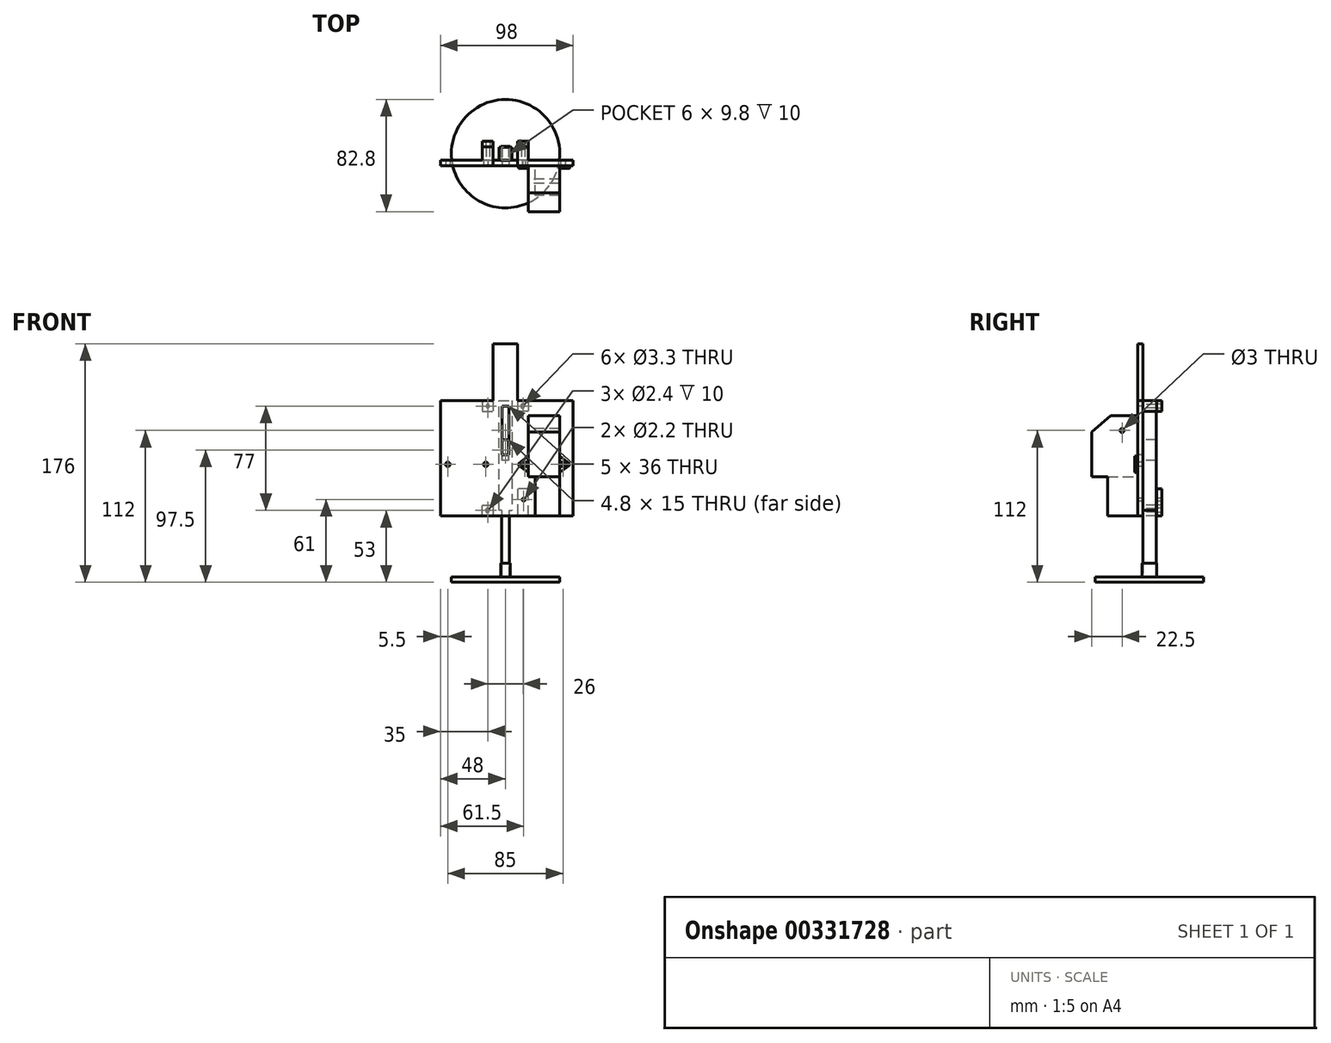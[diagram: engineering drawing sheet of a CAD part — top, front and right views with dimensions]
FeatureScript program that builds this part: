
annotation { "Feature Type Name" : "Feature", "Feature Type Description" : "" }
export const myFeature = defineFeature(function(context is Context, id is Id, definition is map)
    precondition{}
    {
        {
            var Q0;
            Q0=qCreatedBy(makeId("Right.planeOp"),FACE);
            var sketch = newSketch(context, id + "F0", { "sketchPlane" : qUnion([Q0])});
            skLineSegment(sketch, "E0", {"start": v(0, 0) * mm, "end": v(0, 74) * mm});
            skLineSegment(sketch, "E1", {"start": v(0, 74) * mm, "end": v(-20, 74) * mm});
            skLineSegment(sketch, "E2", {"start": v(-20, 74) * mm, "end": v(-34, 74) * mm, "construction": true});
            skLineSegment(sketch, "E3", {"start": v(-34, 74) * mm, "end": v(-34, 73) * mm, "construction": true});
            skLineSegment(sketch, "E4", {"start": v(-34, 73) * mm, "end": v(-34, 62) * mm, "construction": true});
            skLineSegment(sketch, "E5", {"start": v(-34, 62) * mm, "end": v(-20, 74) * mm});
            skLineSegment(sketch, "E6", {"start": v(-34, 62) * mm, "end": v(-34, 29) * mm});
            skLineSegment(sketch, "E7", {"start": v(-34, 29) * mm, "end": v(-22, 29) * mm});
            skLineSegment(sketch, "E8", {"start": v(-22, 29) * mm, "end": v(-22, 0) * mm});
            skLineSegment(sketch, "E9", {"start": v(-22, 0) * mm, "end": v(0, 0) * mm});
            skLineSegment(sketch, "E10", {"start": v(0, 74) * mm, "end": v(-11.5, 74) * mm, "construction": true});
            skLineSegment(sketch, "E11", {"start": v(-11.5, 74) * mm, "end": v(-11.5, 63) * mm, "construction": true});
            skCircle(sketch, "E12", {"center": v(-11.5, 63) * mm, "radius": 1.5 * mm});
            skSolve(sketch);
        }
        {
            var Q0;
            Q0 = qSketchRegion(id + "F0", true);
            extrude(context, id + "F1", {"entities" : qUnion([Q0]), "depth" : 23 * mm});
        }
        {
            var Q0;
            Q0=makeQuery(id+"F1.opExtrude","CAP_FACE",FACE,{"disambiguationData":[OSD([sQuery(id+"F0.wireOp",EDGE,"E0"),sQuery(id+"F0.wireOp",EDGE,"E1"),sQuery(id+"F0.wireOp",EDGE,"E5"),sQuery(id+"F0.wireOp",EDGE,"E6"),sQuery(id+"F0.wireOp",EDGE,"E7"),sQuery(id+"F0.wireOp",EDGE,"E8"),sQuery(id+"F0.wireOp",EDGE,"E9"),sQuery(id+"F0.wireOp",EDGE,"E12")])],"isStart":true});
            var sketch = newSketch(context, id + "F2", { "sketchPlane" : qUnion([Q0])});
            skLineSegment(sketch, "E13", {"start": v(22, 29) * mm, "end": v(0, 29) * mm});
            skLineSegment(sketch, "E14", {"start": v(0, 29) * mm, "end": v(0, 0) * mm});
            skLineSegment(sketch, "E15", {"start": v(0, 0) * mm, "end": v(22, 0) * mm});
            skLineSegment(sketch, "E16", {"start": v(22, 0) * mm, "end": v(22, 29) * mm});
            skSolve(sketch);
        }
        {
            var Q0;
            Q0 = qSketchRegion(id + "F2", true);
            extrude(context, id + "F3", {"entities" : qUnion([Q0]), "operationType" : NewBodyOperationType.REMOVE, "oppositeDirection" : true, "depth" : 5 * mm});
        }
        {
            var Q0;
            Q0=makeQuery(id+"F1.opExtrude","SWEPT_FACE",FACE,{"disambiguationData":[OSD([sQuery(id+"F0.wireOp",EDGE,"E0")])]});
            var sketch = newSketch(context, id + "F4", { "sketchPlane" : qUnion([Q0])});
            skLineSegment(sketch, "E17", {"start": v(0, 74) * mm, "end": v(0, 38) * mm, "construction": true});
            skLineSegment(sketch, "E18", {"start": v(0, 38) * mm, "end": v(8, 38) * mm, "construction": true});
            skLineSegment(sketch, "E19", {"start": v(0, 38) * mm, "end": v(-31, 38) * mm, "construction": true});
            skLineSegment(sketch, "E20", {"start": v(0, 38) * mm, "end": v(0, 32) * mm, "construction": true});
            skLineSegment(sketch, "E21", {"start": v(0, 38) * mm, "end": v(0, 44) * mm, "construction": true});
            skLineSegment(sketch, "E22", {"start": v(-23, 38) * mm, "end": v(-23, 44) * mm, "construction": true});
            skLineSegment(sketch, "E23", {"start": v(-23, 38) * mm, "end": v(-23, 32) * mm, "construction": true});
            skLineSegment(sketch, "E24", {"start": v(-23, 44) * mm, "end": v(-29.93, 38.8) * mm});
            skLineSegment(sketch, "E25", {"start": v(-23, 32) * mm, "end": v(-29.93, 37.2) * mm});
            skLineSegment(sketch, "E26", {"start": v(0, 32) * mm, "end": v(6.93, 37.2) * mm});
            skLineSegment(sketch, "E27", {"start": v(6.93, 38.8) * mm, "end": v(0, 44) * mm});
            skLineSegment(sketch, "E28", {"start": v(-23, 44) * mm, "end": v(-23, 32) * mm});
            skLineSegment(sketch, "E29", {"start": v(0, 44) * mm, "end": v(0, 32) * mm});
            skPoint(sketch, "E30.visualSharp", {"position": v(-31, 38) * mm});
            skArc(sketch, "E30.filletArc", {"start": v(-29.93, 38.8) * mm, "mid": v(-30.33, 38) * mm, "end": v(-29.93, 37.2) * mm});
            skPoint(sketch, "E31.visualSharp", {"position": v(8, 38) * mm});
            skArc(sketch, "E31.filletArc", {"start": v(6.93, 37.2) * mm, "mid": v(7.33, 38) * mm, "end": v(6.93, 38.8) * mm});
            skLineSegment(sketch, "E32", {"start": v(-23, 38) * mm, "end": v(-23, 39.5) * mm, "construction": true});
            skLineSegment(sketch, "E33", {"start": v(-23, 39.5) * mm, "end": v(-28, 39.5) * mm, "construction": true});
            skLineSegment(sketch, "E34", {"start": v(-28, 39.5) * mm, "end": v(-28, 36.5) * mm, "construction": true});
            skLineSegment(sketch, "E35", {"start": v(-28, 36.5) * mm, "end": v(-23, 36.5) * mm, "construction": true});
            skLineSegment(sketch, "E36", {"start": v(-23, 39.5) * mm, "end": v(-28, 39.5) * mm});
            skLineSegment(sketch, "E37", {"start": v(-28, 36.5) * mm, "end": v(-23, 36.5) * mm});
            skLineSegment(sketch, "E38", {"start": v(-28, 36.5) * mm, "end": v(-28, 39.5) * mm});
            skLineSegment(sketch, "E39", {"start": v(0, 38) * mm, "end": v(0, 39.5) * mm, "construction": true});
            skLineSegment(sketch, "E40", {"start": v(0, 38) * mm, "end": v(0, 36.5) * mm, "construction": true});
            skLineSegment(sketch, "E41", {"start": v(0, 39.5) * mm, "end": v(5, 39.5) * mm});
            skLineSegment(sketch, "E42", {"start": v(5, 39.5) * mm, "end": v(5, 36.5) * mm});
            skLineSegment(sketch, "E43", {"start": v(5, 36.5) * mm, "end": v(0, 36.5) * mm});
            skSolve(sketch);
        }
        {
            var Q0;
            {var subQ4=sQuery(id+"F4.wireOp",EDGE,"E26");Q0=makeQuery(id+"F4.imprint","IMPRINT",FACE,{"disambiguationData":[TD([[makeQuery(id+"F4.imprint","IMPRINT",EDGE,{"derivedFrom":subQ4}),1.0]])]});}
            var Q1;
            {var subQ4=sQuery(id+"F4.wireOp",EDGE,"E24");Q1=makeQuery(id+"F4.imprint","IMPRINT",FACE,{"disambiguationData":[TD([[makeQuery(id+"F4.imprint","IMPRINT",EDGE,{"derivedFrom":subQ4}),1.0]])]});}
            extrude(context, id + "F5", {"entities" : qUnion([Q0, Q1]), "operationType" : NewBodyOperationType.ADD, "oppositeDirection" : true, "depth" : 2 * mm});
        }
        {
            var Q0;
            Q0=makeQuery(id+"F5.boolean.opBoolean","MERGE",FACE,{"derivedFrom":[makeQuery(id+"F1.opExtrude","SWEPT_FACE",FACE,{"disambiguationData":[OSD([sQuery(id+"F0.wireOp",EDGE,"E0")])]}),makeQuery(id+"F5.opExtrude","CAP_FACE",FACE,{"disambiguationData":[OSD([sQuery(id+"F4.wireOp",EDGE,"E24"),sQuery(id+"F4.wireOp",EDGE,"E25"),sQuery(id+"F4.wireOp",EDGE,"E28"),sQuery(id+"F4.wireOp",EDGE,"E30.filletArc"),sQuery(id+"F4.wireOp",EDGE,"E36"),sQuery(id+"F4.wireOp",EDGE,"E37"),sQuery(id+"F4.wireOp",EDGE,"E38")])],"isStart":true}),makeQuery(id+"F5.opExtrude","CAP_FACE",FACE,{"disambiguationData":[OSD([sQuery(id+"F4.wireOp",EDGE,"E26"),sQuery(id+"F4.wireOp",EDGE,"E27"),sQuery(id+"F4.wireOp",EDGE,"E29"),sQuery(id+"F4.wireOp",EDGE,"E31.filletArc"),sQuery(id+"F4.wireOp",EDGE,"E41"),sQuery(id+"F4.wireOp",EDGE,"E42"),sQuery(id+"F4.wireOp",EDGE,"E43")])],"isStart":true})]});
            var sketch = newSketch(context, id + "F6", { "sketchPlane" : qUnion([Q0])});
            skLineSegment(sketch, "E44", {"start": v(-29.93, 38.8) * mm, "end": v(-29.93, 37.2) * mm, "construction": true});
            skLineSegment(sketch, "E45", {"start": v(-29.93, 37.2) * mm, "end": v(-29.93, 38) * mm, "construction": true});
            skLineSegment(sketch, "E46", {"start": v(-29.93, 38) * mm, "end": v(11.6, 38) * mm, "construction": true});
            skPoint(sketch, "E46.endSnap0", {"position": v(7.33, 38) * mm});
            skLineSegment(sketch, "E47", {"start": v(65, 38) * mm, "end": v(-34.09, 38) * mm, "construction": true});
            skLineSegment(sketch, "E48", {"start": v(0, 74) * mm, "end": v(0, 79) * mm, "construction": true});
            skLineSegment(sketch, "E49", {"start": v(0, 79) * mm, "end": v(17, 79) * mm, "construction": true});
            skLineSegment(sketch, "E50", {"start": v(17, 79) * mm, "end": v(17, -51) * mm, "construction": true});
            skLineSegment(sketch, "E51", {"start": v(17, -51) * mm, "end": v(-33, -51) * mm, "construction": true});
            skLineSegment(sketch, "E52", {"start": v(-33, -51) * mm, "end": v(-33, 79) * mm, "construction": true});
            skLineSegment(sketch, "E53", {"start": v(-33, 79) * mm, "end": v(0, 79) * mm, "construction": true});
            skLineSegment(sketch, "E54.top", {"start": v(-33, 0) * mm, "end": v(65, 0) * mm});
            skLineSegment(sketch, "E54.left", {"start": v(-33, 79) * mm, "end": v(-33, 0) * mm});
            skLineSegment(sketch, "E54.right", {"start": v(65, 85) * mm, "end": v(65, 0) * mm});
            skLineSegment(sketch, "E55", {"start": v(17, 38) * mm, "end": v(2.5, 38) * mm, "construction": true});
            skPoint(sketch, "E55.startSnap0", {"position": v(15.46, 38) * mm});
            skLineSegment(sketch, "E56", {"start": v(2.5, 38) * mm, "end": v(-25.5, 38) * mm, "construction": true});
            skCircle(sketch, "E57", {"center": v(-25.5, 38) * mm, "radius": 1.65 * mm});
            skCircle(sketch, "E58", {"center": v(2.5, 38) * mm, "radius": 1.65 * mm});
            skLineSegment(sketch, "E59", {"start": v(17, 38) * mm, "end": v(31.5, 38) * mm, "construction": true});
            skLineSegment(sketch, "E60", {"start": v(31.5, 38) * mm, "end": v(59.5, 38) * mm, "construction": true});
            skCircle(sketch, "E61", {"center": v(31.5, 38) * mm, "radius": 1.65 * mm});
            skCircle(sketch, "E62", {"center": v(59.5, 38) * mm, "radius": 1.65 * mm});
            skLineSegment(sketch, "E63", {"start": v(0, 74) * mm, "end": v(0, 63) * mm, "construction": true});
            skLineSegment(sketch, "E64", {"start": v(0, 63) * mm, "end": v(17, 63) * mm, "construction": true});
            skLineSegment(sketch, "E65", {"start": v(17, 63) * mm, "end": v(17, 45) * mm, "construction": true});
            skLineSegment(sketch, "E66", {"start": v(17, 63) * mm, "end": v(17, 81) * mm, "construction": true});
            skLineSegment(sketch, "E67", {"start": v(-33, 79) * mm, "end": v(-33, 85) * mm});
            skLineSegment(sketch, "E68", {"start": v(-33, 85) * mm, "end": v(65, 85) * mm});
            skLineSegment(sketch, "E69", {"start": v(17, 81) * mm, "end": v(19.5, 81) * mm});
            skLineSegment(sketch, "E70", {"start": v(17, 45) * mm, "end": v(19.5, 45) * mm});
            skLineSegment(sketch, "E71", {"start": v(19.5, 45) * mm, "end": v(19.5, 81) * mm});
            skLineSegment(sketch, "E72", {"start": v(17, 81) * mm, "end": v(14.5, 81) * mm});
            skLineSegment(sketch, "E73", {"start": v(14.5, 81) * mm, "end": v(14.5, 45) * mm});
            skLineSegment(sketch, "E74", {"start": v(14.5, 45) * mm, "end": v(17, 45) * mm});
            skLineSegment(sketch, "E75", {"start": v(17, 81) * mm, "end": v(17, 85) * mm, "construction": true});
            skLineSegment(sketch, "E76", {"start": v(17, 85) * mm, "end": v(17, 127) * mm, "construction": true});
            skLineSegment(sketch, "E77", {"start": v(17, 127) * mm, "end": v(8, 127) * mm});
            skLineSegment(sketch, "E78", {"start": v(8, 127) * mm, "end": v(8, 85) * mm});
            skLineSegment(sketch, "E79", {"start": v(17, 127) * mm, "end": v(26, 127) * mm});
            skLineSegment(sketch, "E80", {"start": v(26, 127) * mm, "end": v(26, 85) * mm});
            skLineSegment(sketch, "E81", {"start": v(2.5, 38) * mm, "end": v(2.5, 12) * mm, "construction": true});
            skLineSegment(sketch, "E82", {"start": v(2.5, 12) * mm, "end": v(3.5, 12) * mm, "construction": true});
            skCircle(sketch, "E83", {"center": v(3.5, 12) * mm, "radius": 1.1 * mm});
            skSolve(sketch);
        }
        {
            var Q0;
            Q0 = qSketchRegion(id + "F6", true);
            extrude(context, id + "F7", {"entities" : qUnion([Q0]), "depth" : 4 * mm});
        }
        {
            var Q0;
            Q0=makeQuery(id+"F7.opExtrude","CAP_FACE",FACE,{"disambiguationData":[OSD([sQuery(id+"F6.wireOp",EDGE,"E54.top"),sQuery(id+"F6.wireOp",EDGE,"E54.left"),sQuery(id+"F6.wireOp",EDGE,"E54.right"),sQuery(id+"F6.wireOp",EDGE,"E57"),sQuery(id+"F6.wireOp",EDGE,"E58"),sQuery(id+"F6.wireOp",EDGE,"E61"),sQuery(id+"F6.wireOp",EDGE,"E62"),sQuery(id+"F6.wireOp",EDGE,"E67"),sQuery(id+"F6.wireOp",EDGE,"E68"),sQuery(id+"F6.wireOp",EDGE,"E69"),sQuery(id+"F6.wireOp",EDGE,"E70"),sQuery(id+"F6.wireOp",EDGE,"E71"),sQuery(id+"F6.wireOp",EDGE,"E72"),sQuery(id+"F6.wireOp",EDGE,"E73"),sQuery(id+"F6.wireOp",EDGE,"E74"),sQuery(id+"F6.wireOp",EDGE,"E77"),sQuery(id+"F6.wireOp",EDGE,"E78"),sQuery(id+"F6.wireOp",EDGE,"E79"),sQuery(id+"F6.wireOp",EDGE,"E80")])],"isStart":false});
            var sketch = newSketch(context, id + "F8", { "sketchPlane" : qUnion([Q0])});
            skLineSegment(sketch, "E84.bottom", {"start": v(8, 127) * mm, "end": v(26, 127) * mm});
            skLineSegment(sketch, "E84.top", {"start": v(8, 0) * mm, "end": v(26, 0) * mm});
            skLineSegment(sketch, "E84.left", {"start": v(8, 127) * mm, "end": v(8, 0) * mm});
            skLineSegment(sketch, "E84.right", {"start": v(26, 127) * mm, "end": v(26, 0) * mm});
            skLineSegment(sketch, "E85", {"start": v(8, 0) * mm, "end": v(12, 0) * mm, "construction": true});
            skLineSegment(sketch, "E86", {"start": v(26, 0) * mm, "end": v(22, 0) * mm, "construction": true});
            skLineSegment(sketch, "E87", {"start": v(12, 0) * mm, "end": v(12, 123) * mm});
            skLineSegment(sketch, "E88", {"start": v(12, 123) * mm, "end": v(22, 123) * mm});
            skLineSegment(sketch, "E89", {"start": v(22, 123) * mm, "end": v(22, 0) * mm});
            skLineSegment(sketch, "E90", {"start": v(26, 85) * mm, "end": v(34, 85) * mm});
            skLineSegment(sketch, "E91", {"start": v(34, 85) * mm, "end": v(34, 77) * mm});
            skLineSegment(sketch, "E92", {"start": v(34, 77) * mm, "end": v(26, 77) * mm});
            skLineSegment(sketch, "E93", {"start": v(8, 85) * mm, "end": v(0, 85) * mm});
            skLineSegment(sketch, "E94", {"start": v(0, 85) * mm, "end": v(0, 77) * mm});
            skLineSegment(sketch, "E95", {"start": v(0, 77) * mm, "end": v(8, 77) * mm});
            skLineSegment(sketch, "E96", {"start": v(26, 0) * mm, "end": v(34, 0) * mm});
            skLineSegment(sketch, "E97", {"start": v(34, 0) * mm, "end": v(34, 8) * mm});
            skLineSegment(sketch, "E98", {"start": v(34, 8) * mm, "end": v(26, 8) * mm});
            skLineSegment(sketch, "E99", {"start": v(8, 8) * mm, "end": v(8, 4) * mm, "construction": true});
            skCircle(sketch, "E100", {"center": v(30, 4) * mm, "radius": 1.2 * mm});
            skLineSegment(sketch, "E101", {"start": v(26, 77) * mm, "end": v(30, 77) * mm, "construction": true});
            skLineSegment(sketch, "E102", {"start": v(30, 77) * mm, "end": v(30, 81) * mm, "construction": true});
            skLineSegment(sketch, "E103", {"start": v(30, 81) * mm, "end": v(4, 81) * mm, "construction": true});
            skCircle(sketch, "E104", {"center": v(4, 81) * mm, "radius": 1.2 * mm});
            skCircle(sketch, "E105", {"center": v(30, 81) * mm, "radius": 1.2 * mm});
            skLineSegment(sketch, "E106", {"start": v(12, 0) * mm, "end": v(14, 0) * mm});
            skLineSegment(sketch, "E107", {"start": v(14, 0) * mm, "end": v(14, 4) * mm});
            skLineSegment(sketch, "E108", {"start": v(14, 4) * mm, "end": v(12, 4) * mm});
            skLineSegment(sketch, "E109", {"start": v(22, 0) * mm, "end": v(20, 0) * mm});
            skLineSegment(sketch, "E110", {"start": v(20, 0) * mm, "end": v(20, 4) * mm});
            skLineSegment(sketch, "E111", {"start": v(20, 4) * mm, "end": v(22, 4) * mm});
            skSolve(sketch);
        }
        {
            var Q0;
            {var subQ1=sQuery(id+"F8.wireOp",EDGE,"E84.bottom");Q0=makeQuery(id+"F8.imprint","IMPRINT",FACE,{"disambiguationData":[TD([[makeQuery(id+"F8.imprint","IMPRINT",EDGE,{"derivedFrom":subQ1}),-1.0]])]});}
            var Q1;
            {var subQ1=sQuery(id+"F8.wireOp",EDGE,"E90");Q1=makeQuery(id+"F8.imprint","IMPRINT",FACE,{"disambiguationData":[TD([[makeQuery(id+"F8.imprint","IMPRINT",EDGE,{"derivedFrom":subQ1}),-1.0]])]});}
            var Q2;
            {var subQ0=sQuery(id+"F8.wireOp",EDGE,"E93");Q2=makeQuery(id+"F8.imprint","IMPRINT",FACE,{"disambiguationData":[TD([[makeQuery(id+"F8.imprint","IMPRINT",EDGE,{"derivedFrom":subQ0}),-1.0]])]});}
            var Q3;
            {var subQ1=sQuery(id+"F8.wireOp",EDGE,"0Vjj4xsE-PBRp-m6nF-p9aE-0DxyDTZXc8iU");Q3=makeQuery(id+"F8.imprint","IMPRINT",FACE,{"disambiguationData":[TD([[makeQuery(id+"F8.imprint","IMPRINT",EDGE,{"derivedFrom":subQ1}),1.0]])]});}
            var Q4;
            {var subQ1=sQuery(id+"F8.wireOp",EDGE,"E96");Q4=makeQuery(id+"F8.imprint","IMPRINT",FACE,{"disambiguationData":[TD([[makeQuery(id+"F8.imprint","IMPRINT",EDGE,{"derivedFrom":subQ1}),1.0]])]});}
            var Q5;
            {var subQ0=sQuery(id+"F8.wireOp",EDGE,"E106");Q5=makeQuery(id+"F8.imprint","IMPRINT",FACE,{"disambiguationData":[TD([[makeQuery(id+"F8.imprint","IMPRINT",EDGE,{"derivedFrom":subQ0}),1.0]])]});}
            var Q6;
            {var subQ0=sQuery(id+"F8.wireOp",EDGE,"E109");Q6=makeQuery(id+"F8.imprint","IMPRINT",FACE,{"disambiguationData":[TD([[makeQuery(id+"F8.imprint","IMPRINT",EDGE,{"derivedFrom":subQ0}),1.0]])]});}
            extrude(context, id + "F9", {"entities" : qUnion([Q0, Q1, Q2, Q3, Q4, Q5, Q6]), "operationType" : NewBodyOperationType.ADD, "depth" : 10 * mm});
        }
        {
            var Q0;
            Q0=makeQuery(id+"F9.opExtrude","CAP_FACE",FACE,{"disambiguationData":[OSD([sQuery(id+"F8.wireOp",EDGE,"E84.bottom"),sQuery(id+"F8.wireOp",EDGE,"E84.top"),sQuery(id+"F8.wireOp",EDGE,"E84.left"),sQuery(id+"F8.wireOp",EDGE,"E84.right"),sQuery(id+"F8.wireOp",EDGE,"E87"),sQuery(id+"F8.wireOp",EDGE,"E88"),sQuery(id+"F8.wireOp",EDGE,"E89"),sQuery(id+"F8.wireOp",EDGE,"E90"),sQuery(id+"F8.wireOp",EDGE,"E91"),sQuery(id+"F8.wireOp",EDGE,"E92"),sQuery(id+"F8.wireOp",EDGE,"E93"),sQuery(id+"F8.wireOp",EDGE,"E94"),sQuery(id+"F8.wireOp",EDGE,"E95"),sQuery(id+"F8.wireOp",EDGE,"E96"),sQuery(id+"F8.wireOp",EDGE,"E97"),sQuery(id+"F8.wireOp",EDGE,"E98"),sQuery(id+"F8.wireOp",EDGE,"0Vjj4xsE-PBRp-m6nF-p9aE-0DxyDTZXc8iU"),sQuery(id+"F8.wireOp",EDGE,"ORjWw6Pk-xSS7-amy0-CIca-kRkBNEQwT6SR"),sQuery(id+"F8.wireOp",EDGE,"eKynJURx-tOQH-tVT4-Dyi6-oZPY2QAyEPxH"),sQuery(id+"F8.wireOp",EDGE,"1UhUEwTt-POgJ-JUpx-qXra-FbP34R6efhTE"),sQuery(id+"F8.wireOp",EDGE,"E100"),sQuery(id+"F8.wireOp",EDGE,"E104"),sQuery(id+"F8.wireOp",EDGE,"E105"),sQuery(id+"F8.wireOp",EDGE,"E106"),sQuery(id+"F8.wireOp",EDGE,"E107"),sQuery(id+"F8.wireOp",EDGE,"E108"),sQuery(id+"F8.wireOp",EDGE,"E109"),sQuery(id+"F8.wireOp",EDGE,"E110"),sQuery(id+"F8.wireOp",EDGE,"E111")])],"isStart":false});
            var sketch = newSketch(context, id + "F10", { "sketchPlane" : qUnion([Q0])});
            skLineSegment(sketch, "E112", {"start": v(8, 0) * mm, "end": v(34, 0) * mm});
            skLineSegment(sketch, "E113", {"start": v(34, 0) * mm, "end": v(34, 8) * mm});
            skLineSegment(sketch, "E114", {"start": v(34, 8) * mm, "end": v(26, 8) * mm});
            skLineSegment(sketch, "E115", {"start": v(26, 8) * mm, "end": v(26, 77) * mm});
            skLineSegment(sketch, "E116", {"start": v(26, 77) * mm, "end": v(34, 77) * mm});
            skLineSegment(sketch, "E117", {"start": v(34, 77) * mm, "end": v(34, 85) * mm});
            skLineSegment(sketch, "E118", {"start": v(34, 85) * mm, "end": v(26, 85) * mm});
            skLineSegment(sketch, "E119", {"start": v(26, 85) * mm, "end": v(26, 127) * mm});
            skLineSegment(sketch, "E120", {"start": v(26, 127) * mm, "end": v(8, 127) * mm});
            skLineSegment(sketch, "E121", {"start": v(8, 127) * mm, "end": v(8, 85) * mm});
            skLineSegment(sketch, "E122", {"start": v(8, 85) * mm, "end": v(0, 85) * mm});
            skLineSegment(sketch, "E123", {"start": v(0, 85) * mm, "end": v(0, 77) * mm});
            skLineSegment(sketch, "E124", {"start": v(0, 77) * mm, "end": v(8, 77) * mm});
            skLineSegment(sketch, "E125", {"start": v(8, 77) * mm, "end": v(8, 127) * mm});
            skLineSegment(sketch, "E126", {"start": v(8, 127) * mm, "end": v(8, 127) * mm});
            skLineSegment(sketch, "E127", {"start": v(34, 0) * mm, "end": v(8, 0) * mm});
            skCircle(sketch, "E128", {"center": v(30, 4) * mm, "radius": 1.65 * mm});
            skCircle(sketch, "E129", {"center": v(30, 81) * mm, "radius": 1.65 * mm});
            skCircle(sketch, "E130", {"center": v(4, 81) * mm, "radius": 1.65 * mm});
            skLineSegment(sketch, "E131", {"start": v(26, 85) * mm, "end": v(26, 77) * mm});
            skLineSegment(sketch, "E132", {"start": v(26, 8) * mm, "end": v(26, 0) * mm});
            skLineSegment(sketch, "E133.bottom", {"start": v(8, 127) * mm, "end": v(26, 127) * mm});
            skLineSegment(sketch, "E133.top", {"start": v(8, 0) * mm, "end": v(26, 0) * mm});
            skLineSegment(sketch, "E133.left", {"start": v(8, 127) * mm, "end": v(8, 0) * mm});
            skLineSegment(sketch, "E133.right", {"start": v(26, 127) * mm, "end": v(26, 0) * mm});
            skLineSegment(sketch, "E134", {"start": v(8, 0) * mm, "end": v(0, 0) * mm});
            skLineSegment(sketch, "E135", {"start": v(0, 0) * mm, "end": v(0, 20) * mm});
            skLineSegment(sketch, "E136", {"start": v(0, 20) * mm, "end": v(8, 20) * mm});
            skLineSegment(sketch, "E137", {"start": v(14, 0) * mm, "end": v(17, 0) * mm, "construction": true});
            skLineSegment(sketch, "E138", {"start": v(17, 0) * mm, "end": v(17, 12) * mm, "construction": true});
            skLineSegment(sketch, "E139", {"start": v(17, 12) * mm, "end": v(3.5, 12) * mm, "construction": true});
            skCircle(sketch, "E140", {"center": v(3.5, 12) * mm, "radius": 1.1 * mm});
            skSolve(sketch);
        }
        {
            var Q0;
            Q0=makeQuery(id+"F10.imprint","IMPRINT",FACE,{"disambiguationData":[TD([[makeQuery(id+"F10.imprint","IMPRINT",EDGE,{"derivedFrom":makeQuery(id+"F9.opExtrude","CAP_EDGE",EDGE,{"disambiguationData":[OSD([sQuery(id+"F8.wireOp",EDGE,"E87")])],"isStart":false})}),-1.0]])]});
            var Q1;
            Q1=makeQuery(id+"F10.imprint","IMPRINT",FACE,{"disambiguationData":[TD([[makeQuery(id+"F10.imprint","IMPRINT",EDGE,{"derivedFrom":sQuery(id+"F10.wireOp",EDGE,"E113")}),1.0]])]});
            var Q2;
            {var subQ2=sQuery(id+"F10.wireOp",EDGE,"E116");Q2=makeQuery(id+"F10.imprint","IMPRINT",FACE,{"disambiguationData":[TD([[makeQuery(id+"F10.imprint","IMPRINT",EDGE,{"derivedFrom":subQ2}),-1.0]])]});}
            var Q3;
            {var subQ2=sQuery(id+"F10.wireOp",EDGE,"E122");Q3=makeQuery(id+"F10.imprint","IMPRINT",FACE,{"disambiguationData":[TD([[makeQuery(id+"F10.imprint","IMPRINT",EDGE,{"derivedFrom":subQ2}),-1.0]])]});}
            var Q4;
            {var subQ4=sQuery(id+"F10.wireOp",EDGE,"E133.bottom");Q4=makeQuery(id+"F10.imprint","IMPRINT",FACE,{"disambiguationData":[TD([[makeQuery(id+"F10.imprint","IMPRINT",EDGE,{"derivedFrom":subQ4}),-1.0]])]});}
            var Q5;
            {var subQ1=sQuery(id+"F10.wireOp",EDGE,"E134");Q5=makeQuery(id+"F10.imprint","IMPRINT",FACE,{"disambiguationData":[TD([[makeQuery(id+"F10.imprint","IMPRINT",EDGE,{"derivedFrom":subQ1}),-1.0]])]});}
            extrude(context, id + "F11", {"entities" : qUnion([Q0, Q1, Q2, Q3, Q4, Q5]), "depth" : 4 * mm});
        }
        {
            var Q0;
            {var subQ0=sQuery(id+"F6.wireOp",EDGE,"E71");var subQ2=sQuery(id+"F6.wireOp",EDGE,"E73");var subQ3=sQuery(id+"F6.wireOp",EDGE,"E54.top");var subQ4=sQuery(id+"F6.wireOp",EDGE,"E72");var subQ5=sQuery(id+"F6.wireOp",EDGE,"E69");var subQ6=sQuery(id+"F6.wireOp",EDGE,"E74");var subQ7=sQuery(id+"F6.wireOp",EDGE,"E70");Q0=makeQuery(id+"F9.boolean.opBoolean","SPLIT",FACE,{"disambiguationData":[TD([makeQuery(id+"F7.opExtrude","SWEPT_FACE",FACE,{"disambiguationData":[OSD([subQ0])]})])],"derivedFrom":makeQuery(id+"F7.opExtrude","CAP_FACE",FACE,{"disambiguationData":[OSD([subQ3,sQuery(id+"F6.wireOp",EDGE,"E54.left"),sQuery(id+"F6.wireOp",EDGE,"E54.right"),sQuery(id+"F6.wireOp",EDGE,"E57"),sQuery(id+"F6.wireOp",EDGE,"E58"),sQuery(id+"F6.wireOp",EDGE,"E61"),sQuery(id+"F6.wireOp",EDGE,"E62"),sQuery(id+"F6.wireOp",EDGE,"E67"),sQuery(id+"F6.wireOp",EDGE,"E68"),subQ5,subQ7,subQ0,subQ4,subQ2,subQ6,sQuery(id+"F6.wireOp",EDGE,"E77"),sQuery(id+"F6.wireOp",EDGE,"E78"),sQuery(id+"F6.wireOp",EDGE,"E79"),sQuery(id+"F6.wireOp",EDGE,"E80")])],"isStart":false})});}
            var sketch = newSketch(context, id + "F12", { "sketchPlane" : qUnion([Q0])});
            skLineSegment(sketch, "E141", {"start": v(14, 0) * mm, "end": v(12, 0) * mm, "construction": true});
            skLineSegment(sketch, "E142", {"start": v(12, 0) * mm, "end": v(12, 85) * mm, "construction": true});
            skLineSegment(sketch, "E143", {"start": v(12, 85) * mm, "end": v(22, 85) * mm, "construction": true});
            skLineSegment(sketch, "E144", {"start": v(22, 85) * mm, "end": v(22, 0) * mm, "construction": true});
            skLineSegment(sketch, "E145", {"start": v(22, 0) * mm, "end": v(14, 0) * mm, "construction": true});
            skLineSegment(sketch, "E146", {"start": v(12, 4) * mm, "end": v(17, 4) * mm, "construction": true});
            skLineSegment(sketch, "E147", {"start": v(17, 4) * mm, "end": v(17, -58.93) * mm, "construction": true});
            skPoint(sketch, "E148.endSnap0", {"position": v(18, 0) * mm});
            skLineSegment(sketch, "E149", {"start": v(17, 4) * mm, "end": v(17, 128.89) * mm, "construction": true});
            skPoint(sketch, "E149.endSnap0", {"position": v(17, 123) * mm});
            skLineSegment(sketch, "E150", {"start": v(17, 4) * mm, "end": v(12.2, 4) * mm});
            skLineSegment(sketch, "E151", {"start": v(17, 4) * mm, "end": v(21.8, 4) * mm});
            skLineSegment(sketch, "E152", {"start": v(21.8, 4) * mm, "end": v(21.8, 85) * mm});
            skLineSegment(sketch, "E153", {"start": v(21.8, 85) * mm, "end": v(12.2, 85) * mm});
            skLineSegment(sketch, "E154", {"start": v(12.2, 85) * mm, "end": v(12.2, 4) * mm});
            skLineSegment(sketch, "E155", {"start": v(14, 4) * mm, "end": v(14.2, 4) * mm, "construction": true});
            skLineSegment(sketch, "E156", {"start": v(20, 4) * mm, "end": v(19.8, 4) * mm, "construction": true});
            skLineSegment(sketch, "E157", {"start": v(19.8, 4) * mm, "end": v(19.8, -45) * mm});
            skLineSegment(sketch, "E158", {"start": v(19.8, -45) * mm, "end": v(14, -45) * mm});
            skLineSegment(sketch, "E159", {"start": v(14, -45) * mm, "end": v(14.2, 4) * mm});
            skSolve(sketch);
        }
        {
            var Q0;
            Q0 = qSketchRegion(id + "F12", true);
            extrude(context, id + "F13", {"entities" : qUnion([Q0]), "depth" : 9.6 * mm});
        }
        {
            var Q0;
            Q0=makeQuery(id+"F13.opExtrude","CAP_FACE",FACE,{"disambiguationData":[OSD([sQuery(id+"F12.wireOp",EDGE,"E150"),sQuery(id+"F12.wireOp",EDGE,"E151"),sQuery(id+"F12.wireOp",EDGE,"E152"),sQuery(id+"F12.wireOp",EDGE,"E153"),sQuery(id+"F12.wireOp",EDGE,"E154"),sQuery(id+"F12.wireOp",EDGE,"E157"),sQuery(id+"F12.wireOp",EDGE,"E158"),sQuery(id+"F12.wireOp",EDGE,"E159")])],"isStart":true});
            var sketch = newSketch(context, id + "F14", { "sketchPlane" : qUnion([Q0])});
            skLineSegment(sketch, "E160", {"start": v(-19.8, 4) * mm, "end": v(-19.8, 56) * mm, "construction": true});
            skLineSegment(sketch, "E161", {"start": v(-14.2, 4) * mm, "end": v(-14.2, 56) * mm, "construction": true});
            skLineSegment(sketch, "E162", {"start": v(-19.8, 56) * mm, "end": v(-19.4, 56) * mm, "construction": true});
            skLineSegment(sketch, "E163.bottom", {"start": v(-19.4, 56) * mm, "end": v(-14.6, 56) * mm});
            skLineSegment(sketch, "E163.top", {"start": v(-19.4, 41) * mm, "end": v(-14.6, 41) * mm});
            skLineSegment(sketch, "E163.left", {"start": v(-19.4, 56) * mm, "end": v(-19.4, 41) * mm});
            skLineSegment(sketch, "E163.right", {"start": v(-14.6, 56) * mm, "end": v(-14.6, 41) * mm});
            skSolve(sketch);
        }
        {
            var Q0;
            Q0=makeQuery(id+"F14.imprint","IMPRINT",FACE,{"disambiguationData":[TD([[makeQuery(id+"F14.imprint","IMPRINT",EDGE,{"derivedFrom":sQuery(id+"F14.wireOp",EDGE,"E163.bottom")}),-1.0]])]});
            extrude(context, id + "F15", {"entities" : qUnion([Q0]), "operationType" : NewBodyOperationType.REMOVE, "oppositeDirection" : true, "depth" : 25 * mm});
        }
        {
            var Q0;
            Q0=makeQuery(id+"F13.opExtrude","SWEPT_FACE",FACE,{"disambiguationData":[OSD([sQuery(id+"F12.wireOp",EDGE,"E158")])]});
            var sketch = newSketch(context, id + "F16", { "sketchPlane" : qUnion([Q0])});
            skLineSegment(sketch, "E164", {"start": v(-19.8, -4) * mm, "end": v(-14, -13.6) * mm, "construction": true});
            skLineSegment(sketch, "E165", {"start": v(-14, -4) * mm, "end": v(-19.8, -13.6) * mm, "construction": true});
            skCircle(sketch, "E166", {"center": v(-16.9, -8.8) * mm, "radius": 40 * mm});
            skSolve(sketch);
        }
        {
            var Q0;
            Q0 = qSketchRegion(id + "F16", true);
            extrude(context, id + "F17", {"entities" : qUnion([Q0]), "depth" : 4 * mm});
        }
        {
            var Q0;
            Q0=makeQuery(id+"F17.opExtrude","CAP_FACE",FACE,{"disambiguationData":[OSD([sQuery(id+"F16.wireOp",EDGE,"E166")])],"isStart":true});
            var sketch = newSketch(context, id + "F18", { "sketchPlane" : qUnion([Q0])});
            skLineSegment(sketch, "E167.bottom", {"start": v(-19.9, 13.7) * mm, "end": v(-13.9, 13.7) * mm});
            skLineSegment(sketch, "E167.top", {"start": v(-19.9, 3.9) * mm, "end": v(-13.9, 3.9) * mm});
            skLineSegment(sketch, "E167.left", {"start": v(-19.9, 13.7) * mm, "end": v(-19.9, 3.9) * mm});
            skLineSegment(sketch, "E167.right", {"start": v(-13.9, 13.7) * mm, "end": v(-13.9, 3.9) * mm});
            skPoint(sketch, "E167.middle", {"position": v(-16.9, 8.8) * mm});
            skLineSegment(sketch, "E168.bottom", {"start": v(-20.4, 14.2) * mm, "end": v(-13.4, 14.2) * mm});
            skLineSegment(sketch, "E168.top", {"start": v(-20.4, 3.4) * mm, "end": v(-13.4, 3.4) * mm});
            skLineSegment(sketch, "E168.left", {"start": v(-20.4, 14.2) * mm, "end": v(-20.4, 3.4) * mm});
            skLineSegment(sketch, "E168.right", {"start": v(-13.4, 14.2) * mm, "end": v(-13.4, 3.4) * mm});
            skSolve(sketch);
        }
        {
            var Q0;
            Q0 = qSketchRegion(id + "F18", true);
            extrude(context, id + "F19", {"entities" : qUnion([Q0]), "operationType" : NewBodyOperationType.ADD, "depth" : 10 * mm});
        }
        {
            var Q0;
            Q0=makeQuery(id+"F9.opExtrude","CAP_FACE",FACE,{"disambiguationData":[OSD([sQuery(id+"F8.wireOp",EDGE,"E84.bottom"),sQuery(id+"F8.wireOp",EDGE,"E84.top"),sQuery(id+"F8.wireOp",EDGE,"E84.left"),sQuery(id+"F8.wireOp",EDGE,"E84.right"),sQuery(id+"F8.wireOp",EDGE,"E87"),sQuery(id+"F8.wireOp",EDGE,"E88"),sQuery(id+"F8.wireOp",EDGE,"E89"),sQuery(id+"F8.wireOp",EDGE,"E90"),sQuery(id+"F8.wireOp",EDGE,"E91"),sQuery(id+"F8.wireOp",EDGE,"E92"),sQuery(id+"F8.wireOp",EDGE,"E93"),sQuery(id+"F8.wireOp",EDGE,"E94"),sQuery(id+"F8.wireOp",EDGE,"E95"),sQuery(id+"F8.wireOp",EDGE,"E96"),sQuery(id+"F8.wireOp",EDGE,"E97"),sQuery(id+"F8.wireOp",EDGE,"E98"),sQuery(id+"F8.wireOp",EDGE,"E100"),sQuery(id+"F8.wireOp",EDGE,"E104"),sQuery(id+"F8.wireOp",EDGE,"E105"),sQuery(id+"F8.wireOp",EDGE,"E106"),sQuery(id+"F8.wireOp",EDGE,"E107"),sQuery(id+"F8.wireOp",EDGE,"E108"),sQuery(id+"F8.wireOp",EDGE,"E109"),sQuery(id+"F8.wireOp",EDGE,"E110"),sQuery(id+"F8.wireOp",EDGE,"E111")])],"isStart":false});
            var sketch = newSketch(context, id + "F20", { "sketchPlane" : qUnion([Q0])});
            skLineSegment(sketch, "E169", {"start": v(8, 0) * mm, "end": v(8, 27) * mm, "construction": true});
            skLineSegment(sketch, "E170", {"start": v(8, 27) * mm, "end": v(12, 27) * mm});
            skLineSegment(sketch, "E171", {"start": v(12, 27) * mm, "end": v(12, 17) * mm});
            skLineSegment(sketch, "E172", {"start": v(12, 17) * mm, "end": v(8, 17) * mm});
            skLineSegment(sketch, "E173", {"start": v(8, 17) * mm, "end": v(8, 27) * mm});
            skSolve(sketch);
        }
        {
            var Q0;
            Q0 = qSketchRegion(id + "F20", true);
            extrude(context, id + "F21", {"entities" : qUnion([Q0]), "operationType" : NewBodyOperationType.REMOVE, "oppositeDirection" : true, "depth" : 10 * mm});
        }
    });
